# Revit family: Shower_System-Delta-Vero-Roman
name_source: partatom
category: Plumbing Fixtures
revit_build: Autodesk Revit MEP 2012 (Build: 20110916_2132(x64)
units: mm (PartAtom-declared; Revit-internal decimal feet)

## types (8) — shared parameters
Date Modified = July 17, 2015
Default Elevation = 48 "
Depth = 10 "
Equipment Abbreviation = RT
Family Version = 1.0
Manufacturer = Delta Faucet Company
Model Disclaimer = Contact Delta Faucet Company for More Information
Product Documentation Link = http://www.deltafaucet.com
Product Page URL = http://www.deltafaucet.com
URL = http://www.deltafaucet.com
Width = 7.075 "
z Height = 10 "
z Width = 7.075 "
zero-valued in all types: z Offset

## per-type parameters (varying)
| type | Description | Model | Product Material | z Tub Spout Visible | z Type |
| Chrome | Vero Monitor Series Tub and Shower Trim, Chrome | T14453 | Chrome - Delta - Polished | Yes | 1 |
| Champagne Bronze | Vero Monitor Series Tub and Shower Trim, Champagne Bronze | T14453-CZ | Bronze - Delta - Champagne | Yes | 2 |
| Venetian Bronze | Vero Monitor Series Tub and Shower Trim, Venetian Bronze | T14453-RB | Bronze - Delta - Venetian | Yes | 3 |
| Stainless | Vero Monitor Series Tub and Shower Trim, Stainless | T14453-SS | Stainless Steel - Delta - Polished | Yes | 4 |
| Chrome, Without Tub Spout | Vero Monitor Series Shower Trim, Chrome | T14253 | Chrome - Delta - Polished | No | 12 |
| Champagne Bronze, Without Tub Spout | Vero Monitor Series Shower Trim, Champagne Bronze | T14253-CZ | Bronze - Delta - Champagne | No | 22 |
| Stainless, Without Tub Spout | Vero Monitor Series Shower Trim, Stainless | T14253-SS | Stainless Steel - Delta - Polished | No | 42 |
| Venetian Bronze, Without Tub Spout | Vero Monitor Series Shower Trim, Venetian Bronze | T14253-RB | Bronze - Delta - Venetian | No | 32 |

## geometry (parser evidence)
native form markers: Blend x8, Sweep x2
no freeform markers — native parametric forms only
